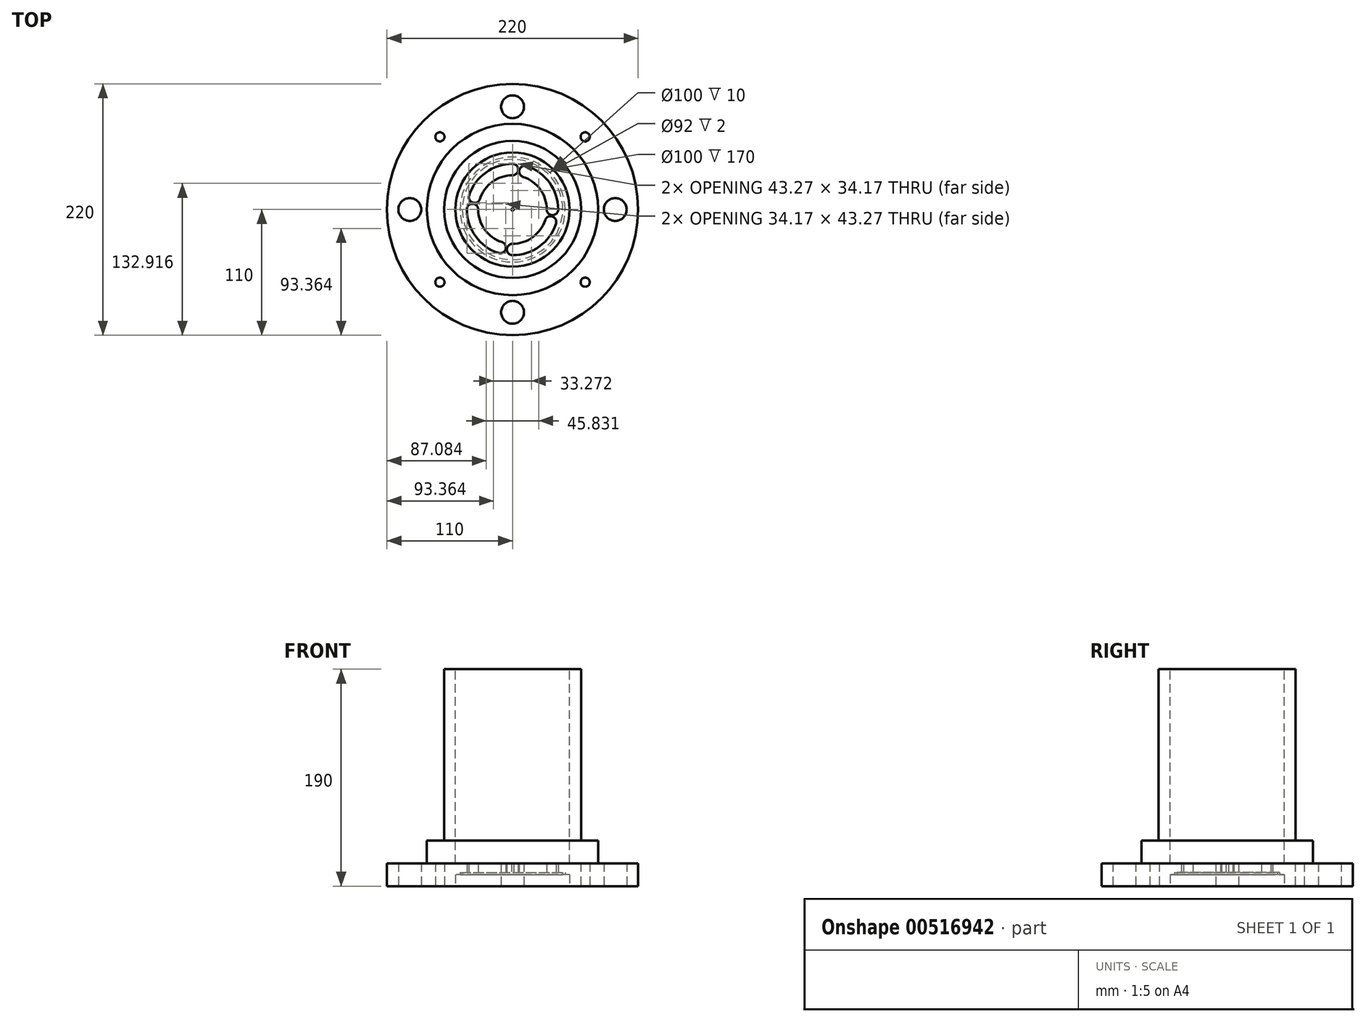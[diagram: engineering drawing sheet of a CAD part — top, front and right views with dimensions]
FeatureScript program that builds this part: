
annotation { "Feature Type Name" : "Feature", "Feature Type Description" : "" }
export const myFeature = defineFeature(function(context is Context, id is Id, definition is map)
    precondition{}
    {
        {
            var Q0;
            Q0=qCreatedBy(makeId("Front.planeOp"),FACE);
            var sketch = newSketch(context, id + "F0", { "sketchPlane" : qUnion([Q0])});
            skLineSegment(sketch, "E0", {"start": v(110, -20) * mm, "end": v(110, 0) * mm});
            skLineSegment(sketch, "E1", {"start": v(110, 0) * mm, "end": v(0, 0) * mm});
            skLineSegment(sketch, "E2", {"start": v(15, -190) * mm, "end": v(0, -190) * mm});
            skPoint(sketch, "E3.start.orphan", {"position": v(30, -20) * mm});
            skLineSegment(sketch, "E4", {"start": v(0, -190) * mm, "end": v(60, -190) * mm});
            skLineSegment(sketch, "E5", {"start": v(60, -190) * mm, "end": v(60, -40) * mm});
            skLineSegment(sketch, "E6", {"start": v(75, -40) * mm, "end": v(60, -40) * mm});
            skLineSegment(sketch, "E7", {"start": v(75, -40) * mm, "end": v(75, -20) * mm});
            skLineSegment(sketch, "E8.trimOffspring", {"start": v(75, -20) * mm, "end": v(110, -20) * mm});
            skPoint(sketch, "E9.end.orphan", {"position": v(0, -40) * mm});
            skPoint(sketch, "E9.start.orphan", {"position": v(0, -20) * mm});
            skLineSegment(sketch, "E10", {"start": v(0, -190) * mm, "end": v(0, 0) * mm});
            skSolve(sketch);
        }
        {
            var Q0;
            Q0=makeQuery(id+"F0.imprint","IMPRINT",FACE,{"disambiguationData":[TD([[makeQuery(id+"F0.imprint","IMPRINT",EDGE,{"derivedFrom":sQuery(id+"F0.wireOp",EDGE,"E0")}),1.0]])]});
            var Q1;
            Q1=sQuery(id+"F0.wireOp",EDGE,"E10");
            revolve(context, id + "F1", {"entities" : qUnion([Q0]), "axis" : qUnion([Q1]), "revolveType" : RevolveType.FULL});
        }
        {
            var Q0;
            Q0=makeQuery(id+"F1.opRevolve","SWEPT_FACE",FACE,{"disambiguationData":[OSD([sQuery(id+"F0.wireOp",EDGE,"E1")])]});
            cPlane(context, id + "F2", {"entities" : qUnion([Q0]), "cplaneType" : CPlaneType.OFFSET, "offset" : 10 * mm, "oppositeDirection" : true, "width" : 150 * mm, "height" : 150 * mm});
        }
        {
            var Q0;
            Q0=qCreatedBy(makeId("Top.planeOp"),FACE);
            var sketch = newSketch(context, id + "F3", { "sketchPlane" : qUnion([Q0])});
            skLineSegment(sketch, "E11", {"start": v(0, 0) * mm, "end": v(0, 90) * mm});
            skLineSegment(sketch, "E12", {"start": v(0, 0) * mm, "end": v(90, 0) * mm});
            skLineSegment(sketch, "E13", {"start": v(0, 0) * mm, "end": v(0, -90) * mm});
            skLineSegment(sketch, "E14", {"start": v(0, 0) * mm, "end": v(-90, 0) * mm});
            skPoint(sketch, "E15", {"position": v(0, 90) * mm});
            skPoint(sketch, "E16", {"position": v(90, 0) * mm});
            skPoint(sketch, "E17", {"position": v(0, -90) * mm});
            skPoint(sketch, "E18", {"position": v(-90, 0) * mm});
            skSolve(sketch);
        }
        {
            var Q0;
            Q0=sQuery(id+"F3.wireOp",VERTEX,"E15");
            var Q1;
            Q1=sQuery(id+"F3.wireOp",VERTEX,"E16");
            var Q2;
            Q2=sQuery(id+"F3.wireOp",VERTEX,"E17");
            var Q3;
            Q3=sQuery(id+"F3.wireOp",VERTEX,"E18");
            var Q4;
            Q4=makeQuery(id+"F1.opRevolve","SWEPT_BODY",BODY,{"disambiguationData":[OSD([sQuery(id+"F0.wireOp",EDGE,"Bh6ajjMC-5Aix-Ba2f-wDz0-3FlB29rSfbDp"),sQuery(id+"F0.wireOp",EDGE,"E3"),sQuery(id+"F0.wireOp",EDGE,"E0"),sQuery(id+"F0.wireOp",EDGE,"E1")])]});
            hole(context, id + "F4", {"style" : HoleStyle.C_SINK, "endStyle" : HoleEndStyle.BLIND, "holeDiameter" : 20 * mm, "cSinkDiameter" : 20 * mm, "cSinkAngle" : 90 * degree, "holeDepth" : 20 * mm, "isTappedThrough" : true, "tappedDepth" : 12 * mm, "tapClearance" : 3, "startFromSketch" : true, "locations" : qUnion([Q0, Q1, Q2, Q3]), "scope" : qUnion([Q4])});
        }
        {
            var Q0;
            Q0=qCreatedBy(makeId("Top.planeOp"),FACE);
            var sketch = newSketch(context, id + "F5", { "sketchPlane" : qUnion([Q0])});
            skCircle(sketch, "E19", {"center": v(0, 0) * mm, "radius": 50 * mm});
            skSolve(sketch);
        }
        {
            var Q0;
            Q0=makeQuery(id+"F5.imprint","IMPRINT",FACE,{"disambiguationData":[TD([[makeQuery(id+"F5.imprint","IMPRINT",EDGE,{"derivedFrom":sQuery(id+"F5.wireOp",EDGE,"E19")}),1.0]])]});
            extrude(context, id + "F6", {"entities" : qUnion([Q0]), "operationType" : NewBodyOperationType.REMOVE, "oppositeDirection" : true, "depth" : 10 * mm, "offsetDistance" : 25 * mm});
        }
        {
            var Q0;
            Q0=qCreatedBy(makeId("Top.planeOp"),FACE);
            var sketch = newSketch(context, id + "F7", { "sketchPlane" : qUnion([Q0])});
            skCircle(sketch, "E20", {"center": v(0, 0) * mm, "radius": 1 * mm});
            skSolve(sketch);
        }
        {
            var Q0;
            Q0=makeQuery(id+"F7.imprint","IMPRINT",FACE,{"disambiguationData":[TD([[makeQuery(id+"F7.imprint","IMPRINT",EDGE,{"derivedFrom":sQuery(id+"F7.wireOp",EDGE,"E20")}),1.0]])]});
            extrude(context, id + "F8", {"entities" : qUnion([Q0]), "operationType" : NewBodyOperationType.REMOVE, "oppositeDirection" : true, "depth" : 20 * mm, "offsetDistance" : 25 * mm});
        }
        {
            var Q0;
            Q0=qCreatedBy(makeId("Top.planeOp"),FACE);
            var sketch = newSketch(context, id + "F9", { "sketchPlane" : qUnion([Q0])});
            skLineSegment(sketch, "E21", {"start": v(0, 0) * mm, "end": v(90, 0) * mm});
            skCircle(sketch, "E22", {"center": v(63.64, 63.64) * mm, "radius": 4 * mm});
            skCircle(sketch, "E23", {"center": v(63.64, -63.64) * mm, "radius": 4 * mm});
            skCircle(sketch, "E24", {"center": v(-63.64, -63.64) * mm, "radius": 4 * mm});
            skCircle(sketch, "E25", {"center": v(-63.64, 63.64) * mm, "radius": 4 * mm});
            skPoint(sketch, "E26.orphan", {"position": v(0, 90) * mm});
            skSolve(sketch);
        }
        {
            var Q0;
            Q0=makeQuery(id+"F9.imprint","IMPRINT",FACE,{"disambiguationData":[TD([[makeQuery(id+"F9.imprint","IMPRINT",EDGE,{"derivedFrom":sQuery(id+"F9.wireOp",EDGE,"E22")}),1.0]])]});
            var Q1;
            Q1=makeQuery(id+"F9.imprint","IMPRINT",FACE,{"disambiguationData":[TD([[makeQuery(id+"F9.imprint","IMPRINT",EDGE,{"derivedFrom":sQuery(id+"F9.wireOp",EDGE,"E25")}),1.0]])]});
            var Q2;
            Q2=makeQuery(id+"F9.imprint","IMPRINT",FACE,{"disambiguationData":[TD([[makeQuery(id+"F9.imprint","IMPRINT",EDGE,{"derivedFrom":sQuery(id+"F9.wireOp",EDGE,"E24")}),1.0]])]});
            var Q3;
            Q3=makeQuery(id+"F9.imprint","IMPRINT",FACE,{"disambiguationData":[TD([[makeQuery(id+"F9.imprint","IMPRINT",EDGE,{"derivedFrom":sQuery(id+"F9.wireOp",EDGE,"E23")}),1.0]])]});
            extrude(context, id + "F10", {"entities" : qUnion([Q0, Q1, Q2, Q3]), "operationType" : NewBodyOperationType.REMOVE, "oppositeDirection" : true, "depth" : 25 * mm, "offsetDistance" : 25 * mm});
        }
        {
            var Q0;
            Q0=makeQuery(id+"F1.opRevolve","SWEPT_BODY",BODY,{"disambiguationData":[OSD([sQuery(id+"F0.wireOp",EDGE,"Bh6ajjMC-5Aix-Ba2f-wDz0-3FlB29rSfbDp"),sQuery(id+"F0.wireOp",EDGE,"E3"),sQuery(id+"F0.wireOp",EDGE,"E0"),sQuery(id+"F0.wireOp",EDGE,"E1")])]});
            var Q1;
            Q1=qCreatedBy(makeId("Top.planeOp"),FACE);
            mirror(context, id + "F11", {"entities" : qUnion([Q0]), "mirrorPlane" : qUnion([Q1])});
        }
        {
            var Q0;
            Q0=makeQuery(id+"F1.opRevolve","SWEPT_BODY",BODY,{"disambiguationData":[OSD([sQuery(id+"F0.wireOp",EDGE,"Bh6ajjMC-5Aix-Ba2f-wDz0-3FlB29rSfbDp"),sQuery(id+"F0.wireOp",EDGE,"E3"),sQuery(id+"F0.wireOp",EDGE,"E0"),sQuery(id+"F0.wireOp",EDGE,"E1")])]});
            deleteBodies(context, id + "F12", {"entities" : qUnion([Q0])});
        }
        {
            var Q0;
            Q0=makeQuery(id+"F11.opPattern","COPY",FACE,{"derivedFrom":makeQuery(id+"F6.boolean.opBoolean","COPY",FACE,{"derivedFrom":makeQuery(id+"F6.opExtrude","CAP_FACE",FACE,{"disambiguationData":[OSD([sQuery(id+"F5.wireOp",EDGE,"E19")])],"isStart":false})}),"instanceName":"1"});
            cPlane(context, id + "F13", {"entities" : qUnion([Q0]), "cplaneType" : CPlaneType.OFFSET, "offset" : 0 * mm, "oppositeDirection" : true, "width" : 150 * mm, "height" : 150 * mm});
        }
        {
            var Q0;
            Q0=qCreatedBy(id+"F13.planeOp",FACE);
            var sketch = newSketch(context, id + "F14", { "sketchPlane" : qUnion([Q0])});
            skArc(sketch, "E27", {"start": v(-12.36, 38.04) * mm, "mid": v(-32.36, 23.51) * mm, "end": v(-40, 0) * mm});
            skArc(sketch, "E28", {"start": v(-9.27, 28.53) * mm, "mid": v(-6.06, 34.83) * mm, "end": v(-12.36, 38.04) * mm});
            skArc(sketch, "E29", {"start": v(0, 40) * mm, "mid": v(-5, 35) * mm, "end": v(0, 30) * mm});
            skArc(sketch, "E30", {"start": v(28.53, 9.27) * mm, "mid": v(34.83, 6.06) * mm, "end": v(38.04, 12.36) * mm});
            skArc(sketch, "E31", {"start": v(40, 0) * mm, "mid": v(35, 5) * mm, "end": v(30, 0) * mm});
            skArc(sketch, "E32", {"start": v(9.27, -28.53) * mm, "mid": v(6.06, -34.83) * mm, "end": v(12.36, -38.04) * mm});
            skArc(sketch, "E33", {"start": v(0, -40) * mm, "mid": v(5, -35) * mm, "end": v(0, -30) * mm});
            skArc(sketch, "E34", {"start": v(-40, 0) * mm, "mid": v(-35, -5) * mm, "end": v(-30, 0) * mm});
            skArc(sketch, "E35", {"start": v(-28.53, -9.27) * mm, "mid": v(-34.83, -6.06) * mm, "end": v(-38.04, -12.36) * mm});
            skArc(sketch, "E36", {"start": v(-9.27, 28.53) * mm, "mid": v(-24.27, 17.63) * mm, "end": v(-30, 0) * mm});
            skArc(sketch, "E37.trimOffspring", {"start": v(38.04, 12.36) * mm, "mid": v(23.51, 32.36) * mm, "end": v(0, 40) * mm});
            skArc(sketch, "E38.trimOffspring", {"start": v(28.53, 9.27) * mm, "mid": v(17.63, 24.27) * mm, "end": v(0, 30) * mm});
            skArc(sketch, "E39.trimOffspring", {"start": v(9.27, -28.53) * mm, "mid": v(24.27, -17.63) * mm, "end": v(30, 0) * mm});
            skArc(sketch, "E40.trimOffspring", {"start": v(12.36, -38.04) * mm, "mid": v(32.36, -23.51) * mm, "end": v(40, 0) * mm});
            skArc(sketch, "E41.trimOffspring", {"start": v(-38.04, -12.36) * mm, "mid": v(-23.51, -32.36) * mm, "end": v(0, -40) * mm});
            skArc(sketch, "E42.trimOffspring", {"start": v(-28.53, -9.27) * mm, "mid": v(-17.63, -24.27) * mm, "end": v(0, -30) * mm});
            skCircle(sketch, "E43", {"center": v(0, 0) * mm, "radius": 46 * mm});
            skCircle(sketch, "E44", {"center": v(0, 0) * mm, "radius": 44 * mm});
            skSolve(sketch);
        }
        {
            var Q0;
            Q0=makeQuery(id+"F14.imprint","IMPRINT",FACE,{"disambiguationData":[TD([[makeQuery(id+"F14.imprint","IMPRINT",EDGE,{"derivedFrom":sQuery(id+"F14.wireOp",EDGE,"E27")}),1.0]])]});
            var Q1;
            Q1=makeQuery(id+"F14.imprint","IMPRINT",FACE,{"disambiguationData":[TD([[makeQuery(id+"F14.imprint","IMPRINT",EDGE,{"derivedFrom":sQuery(id+"F14.wireOp",EDGE,"E29")}),1.0]])]});
            var Q2;
            Q2=makeQuery(id+"F14.imprint","IMPRINT",FACE,{"disambiguationData":[TD([[makeQuery(id+"F14.imprint","IMPRINT",EDGE,{"derivedFrom":sQuery(id+"F14.wireOp",EDGE,"E31")}),1.0]])]});
            var Q3;
            Q3=makeQuery(id+"F14.imprint","IMPRINT",FACE,{"disambiguationData":[TD([[makeQuery(id+"F14.imprint","IMPRINT",EDGE,{"derivedFrom":sQuery(id+"F14.wireOp",EDGE,"E33")}),1.0]])]});
            extrude(context, id + "F15", {"entities" : qUnion([Q0, Q1, Q2, Q3]), "operationType" : NewBodyOperationType.REMOVE, "oppositeDirection" : true, "depth" : 200 * mm, "offsetDistance" : 25 * mm});
        }
        {
            var Q0;
            Q0=makeQuery(id+"F14.imprint","IMPRINT",FACE,{"disambiguationData":[TD([[makeQuery(id+"F14.imprint","IMPRINT",EDGE,{"derivedFrom":sQuery(id+"F14.wireOp",EDGE,"E43")}),1.0]])]});
            extrude(context, id + "F16", {"entities" : qUnion([Q0]), "operationType" : NewBodyOperationType.REMOVE, "oppositeDirection" : true, "depth" : 2 * mm, "offsetDistance" : 25 * mm});
        }
        {
            var Q0;
            Q0=qCreatedBy(id+"F2.planeOp",FACE);
            cPlane(context, id + "F17", {"entities" : qUnion([Q0]), "cplaneType" : CPlaneType.OFFSET, "offset" : 200 * mm, "width" : 150 * mm, "height" : 150 * mm});
        }
        {
            var Q0;
            Q0=qCreatedBy(id+"F17.planeOp",FACE);
            var sketch = newSketch(context, id + "F18", { "sketchPlane" : qUnion([Q0])});
            skCircle(sketch, "E45", {"center": v(0, 0) * mm, "radius": 50 * mm});
            skSolve(sketch);
        }
        {
            var Q0;
            Q0=qSketchRegion(id+"F18",true);
            extrude(context, id + "F19", {"entities" : qUnion([Q0]), "operationType" : NewBodyOperationType.REMOVE, "oppositeDirection" : true, "depth" : 170 * mm, "offsetDistance" : 25 * mm});
        }
    });
